# Revit family: JOMA_407, 408 & 409
name_source: partatom
category: Structural Connections
revit_build: Autodesk Revit Structure 2012 (Build: 20110309_2315(x64)
units: mm (PartAtom-declared; Revit-internal decimal feet)

## types (3) — shared parameters
Länk Joma Dimensioneringsverktyg = http://www.joma.se
Material = Varmförzinkad stålplåt
b = 40 mm  [stored 0.131234 ft]
t = 3 mm  [stored 0.00984252 ft]
zero-valued in all types: Default Elevation

## per-type parameters (varying)
| type | Typ | Vikt | Vinkelbeslag 407 | Vinkelbeslag 408 | Vinkelbeslag 409 | h | l |
| 4080000 | VINKEL 408 | 0,106 | No | Yes | No | 90 mm  [stored 0.295276 ft] | 35 mm  [stored 0.114829 ft] |
| 4070000 | VINKEL 407 | 0,186 | Yes | No | No | 120 mm  [stored 0.393701 ft] | 90 mm  [stored 0.295276 ft] |
| 4090000 | VINKEL 409 | 0,176 | No | No | Yes | 160 mm  [stored 0.524934 ft] | 50 mm  [stored 0.164042 ft] |

note: [stored X ft] marks values corroborated as IEEE doubles in the binary element streams (Revit-internal decimal feet)

## geometry (parser evidence)
native form markers: Sweep x2
no freeform markers — native parametric forms only
